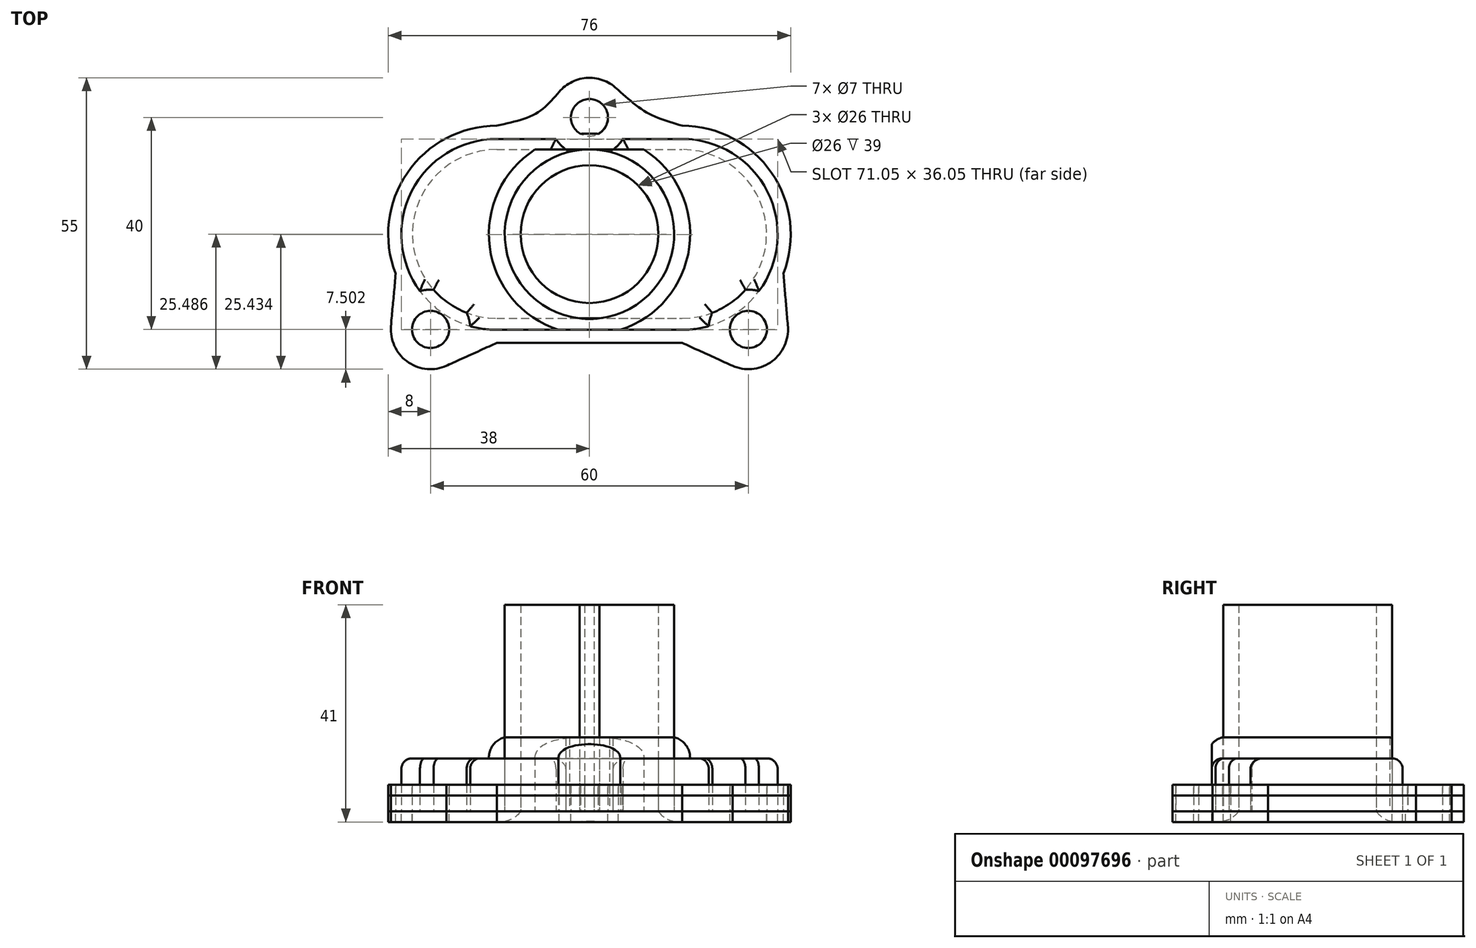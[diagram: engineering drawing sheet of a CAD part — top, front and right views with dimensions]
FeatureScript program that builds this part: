
annotation { "Feature Type Name" : "Feature", "Feature Type Description" : "" }
export const myFeature = defineFeature(function(context is Context, id is Id, definition is map)
    precondition{}
    {
        {
            var Q0;
            Q0=qCreatedBy(makeId("Top.planeOp"),FACE);
            var sketch = newSketch(context, id + "F0", { "sketchPlane" : qUnion([Q0])});
            skCircle(sketch, "E0", {"center": v(0, 24.43) * mm, "radius": 3.5 * mm});
            skCircle(sketch, "E1", {"center": v(30, -15.57) * mm, "radius": 3.5 * mm});
            skCircle(sketch, "E2", {"center": v(-30, -15.57) * mm, "radius": 3.5 * mm});
            skCircle(sketch, "E3", {"center": v(0, 24.43) * mm, "radius": 7.5 * mm});
            skCircle(sketch, "E4", {"center": v(30, -15.57) * mm, "radius": 7.5 * mm});
            skCircle(sketch, "E5", {"center": v(-30, -15.57) * mm, "radius": 7.5 * mm});
            skLineSegment(sketch, "E6", {"start": v(7.34, 22.9) * mm, "end": v(17.5, 22.9) * mm});
            skLineSegment(sketch, "E7", {"start": v(-17.5, -18.1) * mm, "end": v(17.5, -18.1) * mm});
            skLineSegment(sketch, "E8", {"start": v(-7.7, 22.9) * mm, "end": v(-17.5, 22.9) * mm});
            skLineSegment(sketch, "E9", {"start": v(-17.5, 15.9) * mm, "end": v(17.5, 15.9) * mm});
            skLineSegment(sketch, "E10", {"start": v(-17.5, -11.1) * mm, "end": v(17.5, -11.1) * mm});
            skArc(sketch, "E11", {"start": v(17.5, -11.1) * mm, "mid": v(31, 2.4) * mm, "end": v(17.5, 15.9) * mm});
            skArc(sketch, "E12", {"start": v(-17.5, 15.9) * mm, "mid": v(-31, 2.4) * mm, "end": v(-17.5, -11.1) * mm});
            skFitSpline(sketch, "E13", {"points": [v(-17.5, 22.9) * mm, v(-10.03, 25.23) * mm, v(-5.72, 29.28) * mm], "startDerivative": vector(15.12, 3.6) * mm, "endDerivative": vector(8.27, 9.34) * mm});
            skFitSpline(sketch, "E14", {"points": [v(17.5, 22.9) * mm, v(11.1, 25.23) * mm, v(5.4, 29.63) * mm], "startDerivative": vector(-13.33, 4.18) * mm, "endDerivative": vector(-10.87, 9.3) * mm});
            skArc(sketch, "E15", {"start": v(17.5, -18.1) * mm, "mid": v(38, 2.4) * mm, "end": v(17.5, 22.9) * mm});
            skArc(sketch, "E16", {"start": v(-17.5, 22.9) * mm, "mid": v(-38, 2.4) * mm, "end": v(-17.5, -18.1) * mm});
            skFitSpline(sketch, "E17", {"points": [v(27, -22.44) * mm, v(17.5, -18.1) * mm], "startDerivative": vector(-8.6, 4.02) * mm, "endDerivative": vector(-8.6, 4.02) * mm});
            skFitSpline(sketch, "E18", {"points": [v(-17.5, -18.1) * mm, v(-27, -22.44) * mm], "startDerivative": vector(-8, -3.6) * mm, "endDerivative": vector(-8, -3.6) * mm});
            skFitSpline(sketch, "E19", {"points": [v(36.62, -5) * mm, v(37.5, -15.5) * mm], "startDerivative": vector(0.87, -10.65) * mm, "endDerivative": vector(0.87, -10.65) * mm});
            skFitSpline(sketch, "E20", {"points": [v(-37.5, -15.5) * mm, v(-36.62, -5) * mm], "startDerivative": vector(0.62, 11.41) * mm, "endDerivative": vector(0.62, 11.41) * mm});
            skLineSegment(sketch, "E21", {"start": v(-17.5, 20.4) * mm, "end": v(17.5, 20.4) * mm});
            skLineSegment(sketch, "E22", {"start": v(-17.5, -15.66) * mm, "end": v(17.5, -15.66) * mm});
            skArc(sketch, "E23", {"start": v(17.5, -15.66) * mm, "mid": v(35.53, 2.36) * mm, "end": v(17.5, 20.4) * mm});
            skArc(sketch, "E24", {"start": v(-17.5, 20.4) * mm, "mid": v(-35.53, 2.36) * mm, "end": v(-17.5, -15.66) * mm});
            skLineSegment(sketch, "E25", {"start": v(-17.5, 18.4) * mm, "end": v(17.5, 18.4) * mm});
            skLineSegment(sketch, "E26", {"start": v(-17.5, -13.47) * mm, "end": v(17.5, -13.47) * mm});
            skArc(sketch, "E27", {"start": v(17.5, -13.47) * mm, "mid": v(33.43, 2.46) * mm, "end": v(17.5, 18.4) * mm});
            skArc(sketch, "E28", {"start": v(-17.5, 18.4) * mm, "mid": v(-33.43, 2.46) * mm, "end": v(-17.5, -13.47) * mm});
            skCircle(sketch, "E29", {"center": v(0, 2.42) * mm, "radius": 16 * mm});
            skCircle(sketch, "E30", {"center": v(0, 2.42) * mm, "radius": 13 * mm});
            skCircle(sketch, "E31", {"center": v(0, 2.42) * mm, "radius": 19 * mm});
            skSolve(sketch);
        }
        {
            var Q0;
            {var subQ1=sQuery(id+"F0.wireOp",EDGE,"E13");Q0=makeQuery(id+"F0.imprint","IMPRINT",FACE,{"disambiguationData":[TD([[makeQuery(id+"F0.imprint","IMPRINT",EDGE,{"derivedFrom":subQ1}),-1.0]])]});}
            var Q1;
            {var subQ0=sQuery(id+"F0.wireOp",EDGE,"E16");var subQ1=sQuery(id+"F0.wireOp",EDGE,"E2");var subQ2=makeQuery(id+"F0.imprint","INTERSECT",VERTEX,{"disambiguationData":[OD(0.0)],"derivedFrom":[subQ1,subQ0]});Q1=makeQuery(id+"F0.imprint","IMPRINT",FACE,{"disambiguationData":[TD([[makeQuery(id+"F0.imprint","IMPRINT",EDGE,{"disambiguationData":[TD([[subQ2,1.0]])],"derivedFrom":subQ1}),-1.0]])]});}
            var Q2;
            {var subQ6=sQuery(id+"F0.wireOp",EDGE,"E7");Q2=makeQuery(id+"F0.imprint","IMPRINT",FACE,{"disambiguationData":[TD([[makeQuery(id+"F0.imprint","IMPRINT",EDGE,{"derivedFrom":subQ6}),1.0]])]});}
            var Q3;
            {var subQ0=sQuery(id+"F0.wireOp",EDGE,"E18");var subQ1=sQuery(id+"F0.wireOp",EDGE,"E5");var subQ2=makeQuery(id+"F0.imprint","INTERSECT",VERTEX,{"disambiguationData":[OD(1.0)],"derivedFrom":[subQ1,subQ0]});Q3=makeQuery(id+"F0.imprint","IMPRINT",FACE,{"disambiguationData":[TD([[makeQuery(id+"F0.imprint","IMPRINT",EDGE,{"disambiguationData":[TD([[subQ2,-1.0]])],"derivedFrom":subQ1}),-1.0]])]});}
            var Q4;
            {var subQ6=sQuery(id+"F0.wireOp",EDGE,"E16");var subQ10=sQuery(id+"F0.wireOp",EDGE,"E2");var subQ11=makeQuery(id+"F0.imprint","INTERSECT",VERTEX,{"disambiguationData":[OD(0.0)],"derivedFrom":[subQ10,subQ6]});Q4=makeQuery(id+"F0.imprint","IMPRINT",FACE,{"disambiguationData":[TD([[makeQuery(id+"F0.imprint","IMPRINT",EDGE,{"disambiguationData":[TD([[subQ11,-1.0]])],"derivedFrom":subQ10}),-1.0]])]});}
            var Q5;
            {var subQ0=sQuery(id+"F0.wireOp",EDGE,"E20");var subQ1=sQuery(id+"F0.wireOp",EDGE,"E5");var subQ2=makeQuery(id+"F0.imprint","INTERSECT",VERTEX,{"disambiguationData":[OD(1.0)],"derivedFrom":[subQ1,subQ0]});Q5=makeQuery(id+"F0.imprint","IMPRINT",FACE,{"disambiguationData":[TD([[makeQuery(id+"F0.imprint","IMPRINT",EDGE,{"disambiguationData":[TD([[subQ2,1.0]])],"derivedFrom":subQ1}),-1.0]])]});}
            var Q6;
            {var subQ0=sQuery(id+"F0.wireOp",EDGE,"E6");Q6=makeQuery(id+"F0.imprint","IMPRINT",FACE,{"disambiguationData":[TD([[makeQuery(id+"F0.imprint","IMPRINT",EDGE,{"derivedFrom":subQ0}),1.0]])]});}
            var Q7;
            {var subQ0=sQuery(id+"F0.wireOp",EDGE,"E6");Q7=makeQuery(id+"F0.imprint","IMPRINT",FACE,{"disambiguationData":[TD([[makeQuery(id+"F0.imprint","IMPRINT",EDGE,{"derivedFrom":subQ0}),-1.0]])]});}
            var Q8;
            {var subQ0=sQuery(id+"F0.wireOp",EDGE,"E19");var subQ1=sQuery(id+"F0.wireOp",EDGE,"E4");var subQ2=makeQuery(id+"F0.imprint","INTERSECT",VERTEX,{"disambiguationData":[OD(1.0)],"derivedFrom":[subQ1,subQ0]});Q8=makeQuery(id+"F0.imprint","IMPRINT",FACE,{"disambiguationData":[TD([[makeQuery(id+"F0.imprint","IMPRINT",EDGE,{"disambiguationData":[TD([[subQ2,-1.0]])],"derivedFrom":subQ1}),-1.0]])]});}
            var Q9;
            {var subQ6=sQuery(id+"F0.wireOp",EDGE,"E15");var subQ10=sQuery(id+"F0.wireOp",EDGE,"E1");var subQ12=makeQuery(id+"F0.imprint","INTERSECT",VERTEX,{"disambiguationData":[OD(0.0)],"derivedFrom":[subQ10,subQ6]});Q9=makeQuery(id+"F0.imprint","IMPRINT",FACE,{"disambiguationData":[TD([[makeQuery(id+"F0.imprint","IMPRINT",EDGE,{"disambiguationData":[TD([[subQ12,-1.0]])],"derivedFrom":subQ10}),-1.0]])]});}
            var Q10;
            {var subQ0=sQuery(id+"F0.wireOp",EDGE,"E17");var subQ1=sQuery(id+"F0.wireOp",EDGE,"E4");var subQ2=makeQuery(id+"F0.imprint","INTERSECT",VERTEX,{"disambiguationData":[OD(1.0)],"derivedFrom":[subQ1,subQ0]});Q10=makeQuery(id+"F0.imprint","IMPRINT",FACE,{"disambiguationData":[TD([[makeQuery(id+"F0.imprint","IMPRINT",EDGE,{"disambiguationData":[TD([[subQ2,1.0]])],"derivedFrom":subQ1}),-1.0]])]});}
            var Q11;
            {var subQ0=sQuery(id+"F0.wireOp",EDGE,"E15");var subQ5=sQuery(id+"F0.wireOp",EDGE,"E1");var subQ6=makeQuery(id+"F0.imprint","INTERSECT",VERTEX,{"disambiguationData":[OD(0.0)],"derivedFrom":[subQ5,subQ0]});Q11=makeQuery(id+"F0.imprint","IMPRINT",FACE,{"disambiguationData":[TD([[makeQuery(id+"F0.imprint","IMPRINT",EDGE,{"disambiguationData":[TD([[subQ6,1.0]])],"derivedFrom":subQ5}),-1.0]])]});}
            var Q12;
            {var subQ0=sQuery(id+"F0.wireOp",EDGE,"E25");var subQ1=sQuery(id+"F0.wireOp",EDGE,"E3");var subQ2=makeQuery(id+"F0.imprint","INTERSECT",VERTEX,{"disambiguationData":[OD(0.0)],"derivedFrom":[subQ1,subQ0]});Q12=makeQuery(id+"F0.imprint","IMPRINT",FACE,{"disambiguationData":[TD([[makeQuery(id+"F0.imprint","IMPRINT",EDGE,{"disambiguationData":[TD([[subQ2,-1.0]])],"derivedFrom":subQ1}),1.0]])]});}
            var Q13;
            {var subQ0=sQuery(id+"F0.wireOp",EDGE,"E28");var subQ1=sQuery(id+"F0.wireOp",EDGE,"E5");var subQ2=makeQuery(id+"F0.imprint","INTERSECT",VERTEX,{"disambiguationData":[OD(0.0)],"derivedFrom":[subQ1,subQ0]});Q13=makeQuery(id+"F0.imprint","IMPRINT",FACE,{"disambiguationData":[TD([[makeQuery(id+"F0.imprint","IMPRINT",EDGE,{"disambiguationData":[TD([[subQ2,-1.0]])],"derivedFrom":subQ1}),1.0]])]});}
            var Q14;
            {var subQ0=sQuery(id+"F0.wireOp",EDGE,"E27");var subQ1=sQuery(id+"F0.wireOp",EDGE,"E4");var subQ2=makeQuery(id+"F0.imprint","INTERSECT",VERTEX,{"disambiguationData":[OD(0.0)],"derivedFrom":[subQ1,subQ0]});Q14=makeQuery(id+"F0.imprint","IMPRINT",FACE,{"disambiguationData":[TD([[makeQuery(id+"F0.imprint","IMPRINT",EDGE,{"disambiguationData":[TD([[subQ2,-1.0]])],"derivedFrom":subQ1}),1.0]])]});}
            var Q15;
            {var subQ0=sQuery(id+"F0.wireOp",EDGE,"E21");var subQ1=sQuery(id+"F0.wireOp",EDGE,"E3");var subQ2=makeQuery(id+"F0.imprint","INTERSECT",VERTEX,{"disambiguationData":[OD(0.0)],"derivedFrom":[subQ1,subQ0]});Q15=makeQuery(id+"F0.imprint","IMPRINT",FACE,{"disambiguationData":[TD([[makeQuery(id+"F0.imprint","IMPRINT",EDGE,{"disambiguationData":[TD([[subQ2,-1.0]])],"derivedFrom":subQ1}),1.0]])]});}
            var Q16;
            {var subQ0=sQuery(id+"F0.wireOp",EDGE,"E12");Q16=makeQuery(id+"F0.imprint","IMPRINT",FACE,{"disambiguationData":[TD([[makeQuery(id+"F0.imprint","IMPRINT",EDGE,{"derivedFrom":subQ0}),-1.0]])]});}
            var Q17;
            {var subQ0=sQuery(id+"F0.wireOp",EDGE,"E11");Q17=makeQuery(id+"F0.imprint","IMPRINT",FACE,{"disambiguationData":[TD([[makeQuery(id+"F0.imprint","IMPRINT",EDGE,{"derivedFrom":subQ0}),-1.0]])]});}
            var Q18;
            {var subQ0=sQuery(id+"F0.wireOp",EDGE,"E29");var subQ1=sQuery(id+"F0.wireOp",EDGE,"E3");var subQ2=makeQuery(id+"F0.imprint","INTERSECT",VERTEX,{"disambiguationData":[OD(0.0)],"derivedFrom":[subQ1,subQ0]});Q18=makeQuery(id+"F0.imprint","IMPRINT",FACE,{"disambiguationData":[TD([[makeQuery(id+"F0.imprint","IMPRINT",EDGE,{"disambiguationData":[TD([[subQ2,-1.0]])],"derivedFrom":subQ1}),-1.0]])]});}
            var Q19;
            {var subQ0=sQuery(id+"F0.wireOp",EDGE,"E29");var subQ1=sQuery(id+"F0.wireOp",EDGE,"E3");var subQ2=makeQuery(id+"F0.imprint","INTERSECT",VERTEX,{"disambiguationData":[OD(0.0)],"derivedFrom":[subQ1,subQ0]});Q19=makeQuery(id+"F0.imprint","IMPRINT",FACE,{"disambiguationData":[TD([[makeQuery(id+"F0.imprint","IMPRINT",EDGE,{"disambiguationData":[TD([[subQ2,-1.0]])],"derivedFrom":subQ1}),1.0]])]});}
            var Q20;
            {var subQ0=sQuery(id+"F0.wireOp",EDGE,"E29");var subQ1=sQuery(id+"F0.wireOp",EDGE,"E3");var subQ2=makeQuery(id+"F0.imprint","INTERSECT",VERTEX,{"disambiguationData":[OD(1.0)],"derivedFrom":[subQ1,subQ0]});Q20=makeQuery(id+"F0.imprint","IMPRINT",FACE,{"disambiguationData":[TD([[makeQuery(id+"F0.imprint","IMPRINT",EDGE,{"disambiguationData":[TD([[subQ2,-1.0]])],"derivedFrom":subQ1}),1.0]])]});}
            var Q21;
            {var subQ0=sQuery(id+"F0.wireOp",EDGE,"E11");Q21=makeQuery(id+"F0.imprint","IMPRINT",FACE,{"disambiguationData":[TD([[makeQuery(id+"F0.imprint","IMPRINT",EDGE,{"derivedFrom":subQ0}),1.0]])]});}
            var Q22;
            {var subQ0=sQuery(id+"F0.wireOp",EDGE,"E12");Q22=makeQuery(id+"F0.imprint","IMPRINT",FACE,{"disambiguationData":[TD([[makeQuery(id+"F0.imprint","IMPRINT",EDGE,{"derivedFrom":subQ0}),1.0]])]});}
            var Q23;
            Q23=makeQuery(id+"F0.imprint","IMPRINT",FACE,{"disambiguationData":[TD([[makeQuery(id+"F0.imprint","IMPRINT",EDGE,{"derivedFrom":sQuery(id+"F0.wireOp",EDGE,"E30")}),-1.0]])]});
            var Q24;
            {var subQ0=sQuery(id+"F0.wireOp",EDGE,"E29");var subQ1=sQuery(id+"F0.wireOp",EDGE,"E10");var subQ2=makeQuery(id+"F0.imprint","INTERSECT",VERTEX,{"disambiguationData":[OD(0.0)],"derivedFrom":[subQ1,subQ0]});Q24=makeQuery(id+"F0.imprint","IMPRINT",FACE,{"disambiguationData":[TD([[makeQuery(id+"F0.imprint","IMPRINT",EDGE,{"disambiguationData":[TD([[subQ2,-1.0]])],"derivedFrom":subQ1}),-1.0]])]});}
            var Q25;
            {var subQ0=sQuery(id+"F0.wireOp",EDGE,"E31");var subQ1=sQuery(id+"F0.wireOp",EDGE,"E22");var subQ2=makeQuery(id+"F0.imprint","INTERSECT",VERTEX,{"disambiguationData":[OD(0.0)],"derivedFrom":[subQ1,subQ0]});Q25=makeQuery(id+"F0.imprint","IMPRINT",FACE,{"disambiguationData":[TD([[makeQuery(id+"F0.imprint","IMPRINT",EDGE,{"disambiguationData":[TD([[subQ2,-1.0]])],"derivedFrom":subQ1}),-1.0]])]});}
            var Q26;
            {var subQ0=sQuery(id+"F0.wireOp",EDGE,"E29");var subQ1=sQuery(id+"F0.wireOp",EDGE,"E9");var subQ2=makeQuery(id+"F0.imprint","INTERSECT",VERTEX,{"disambiguationData":[OD(1.0)],"derivedFrom":[subQ1,subQ0]});Q26=makeQuery(id+"F0.imprint","IMPRINT",FACE,{"disambiguationData":[TD([[makeQuery(id+"F0.imprint","IMPRINT",EDGE,{"disambiguationData":[TD([[subQ2,-1.0]])],"derivedFrom":subQ1}),-1.0]])]});}
            var Q27;
            {var subQ0=sQuery(id+"F0.wireOp",EDGE,"E31");var subQ1=sQuery(id+"F0.wireOp",EDGE,"E9");var subQ2=makeQuery(id+"F0.imprint","INTERSECT",VERTEX,{"disambiguationData":[OD(0.0)],"derivedFrom":[subQ1,subQ0]});Q27=makeQuery(id+"F0.imprint","IMPRINT",FACE,{"disambiguationData":[TD([[makeQuery(id+"F0.imprint","IMPRINT",EDGE,{"disambiguationData":[TD([[subQ2,-1.0]])],"derivedFrom":subQ1}),-1.0]])]});}
            var Q28;
            {var subQ0=sQuery(id+"F0.wireOp",EDGE,"E31");var subQ1=sQuery(id+"F0.wireOp",EDGE,"E10");var subQ2=makeQuery(id+"F0.imprint","INTERSECT",VERTEX,{"disambiguationData":[OD(0.0)],"derivedFrom":[subQ1,subQ0]});Q28=makeQuery(id+"F0.imprint","IMPRINT",FACE,{"disambiguationData":[TD([[makeQuery(id+"F0.imprint","IMPRINT",EDGE,{"disambiguationData":[TD([[subQ2,-1.0]])],"derivedFrom":subQ1}),-1.0]])]});}
            var Q29;
            {var subQ0=sQuery(id+"F0.wireOp",EDGE,"E29");var subQ1=sQuery(id+"F0.wireOp",EDGE,"E10");var subQ2=makeQuery(id+"F0.imprint","INTERSECT",VERTEX,{"disambiguationData":[OD(1.0)],"derivedFrom":[subQ1,subQ0]});Q29=makeQuery(id+"F0.imprint","IMPRINT",FACE,{"disambiguationData":[TD([[makeQuery(id+"F0.imprint","IMPRINT",EDGE,{"disambiguationData":[TD([[subQ2,-1.0]])],"derivedFrom":subQ1}),-1.0]])]});}
            var Q30;
            {var subQ1=sQuery(id+"F0.wireOp",EDGE,"E3");var subQ7=sQuery(id+"F0.wireOp",EDGE,"E25");var subQ8=makeQuery(id+"F0.imprint","INTERSECT",VERTEX,{"disambiguationData":[OD(0.0)],"derivedFrom":[subQ1,subQ7]});Q30=makeQuery(id+"F0.imprint","IMPRINT",FACE,{"disambiguationData":[TD([[makeQuery(id+"F0.imprint","IMPRINT",EDGE,{"disambiguationData":[TD([[subQ8,-1.0]])],"derivedFrom":subQ1}),-1.0]])]});}
            var Q31;
            {var subQ1=sQuery(id+"F0.wireOp",EDGE,"E3");var subQ5=sQuery(id+"F0.wireOp",EDGE,"E29");var subQ6=makeQuery(id+"F0.imprint","INTERSECT",VERTEX,{"disambiguationData":[OD(1.0)],"derivedFrom":[subQ1,subQ5]});Q31=makeQuery(id+"F0.imprint","IMPRINT",FACE,{"disambiguationData":[TD([[makeQuery(id+"F0.imprint","IMPRINT",EDGE,{"disambiguationData":[TD([[subQ6,-1.0]])],"derivedFrom":subQ1}),-1.0]])]});}
            var Q32;
            {var subQ7=sQuery(id+"F0.wireOp",EDGE,"E31");var subQ8=sQuery(id+"F0.wireOp",EDGE,"E0");var subQ9=makeQuery(id+"F0.imprint","INTERSECT",VERTEX,{"disambiguationData":[OD(0.0)],"derivedFrom":[subQ8,subQ7]});Q32=makeQuery(id+"F0.imprint","IMPRINT",FACE,{"disambiguationData":[TD([[makeQuery(id+"F0.imprint","IMPRINT",EDGE,{"disambiguationData":[TD([[subQ9,-1.0]])],"derivedFrom":subQ8}),-1.0]])]});}
            var Q33;
            {var subQ0=sQuery(id+"F0.wireOp",EDGE,"E31");var subQ1=sQuery(id+"F0.wireOp",EDGE,"E0");var subQ2=makeQuery(id+"F0.imprint","INTERSECT",VERTEX,{"disambiguationData":[OD(0.0)],"derivedFrom":[subQ1,subQ0]});Q33=makeQuery(id+"F0.imprint","IMPRINT",FACE,{"disambiguationData":[TD([[makeQuery(id+"F0.imprint","IMPRINT",EDGE,{"disambiguationData":[TD([[subQ2,1.0]])],"derivedFrom":subQ1}),1.0]])]});}
            var Q34;
            {var subQ0=sQuery(id+"F0.wireOp",EDGE,"E31");var subQ1=sQuery(id+"F0.wireOp",EDGE,"E0");var subQ2=makeQuery(id+"F0.imprint","INTERSECT",VERTEX,{"disambiguationData":[OD(0.0)],"derivedFrom":[subQ1,subQ0]});Q34=makeQuery(id+"F0.imprint","IMPRINT",FACE,{"disambiguationData":[TD([[makeQuery(id+"F0.imprint","IMPRINT",EDGE,{"disambiguationData":[TD([[subQ2,1.0]])],"derivedFrom":subQ1}),-1.0]])]});}
            var Q35;
            {var subQ0=sQuery(id+"F0.wireOp",EDGE,"E29");var subQ1=sQuery(id+"F0.wireOp",EDGE,"E26");var subQ2=makeQuery(id+"F0.imprint","INTERSECT",VERTEX,{"disambiguationData":[OD(0.0)],"derivedFrom":[subQ1,subQ0]});Q35=makeQuery(id+"F0.imprint","IMPRINT",FACE,{"disambiguationData":[TD([[makeQuery(id+"F0.imprint","IMPRINT",EDGE,{"disambiguationData":[TD([[subQ2,-1.0]])],"derivedFrom":subQ1}),-1.0]])]});}
            var Q36;
            {var subQ3=sQuery(id+"F0.wireOp",EDGE,"E5");var subQ5=sQuery(id+"F0.wireOp",EDGE,"E28");var subQ11=makeQuery(id+"F0.imprint","INTERSECT",VERTEX,{"disambiguationData":[OD(0.0)],"derivedFrom":[subQ3,subQ5]});Q36=makeQuery(id+"F0.imprint","IMPRINT",FACE,{"disambiguationData":[TD([[makeQuery(id+"F0.imprint","IMPRINT",EDGE,{"disambiguationData":[TD([[subQ11,1.0]])],"derivedFrom":subQ3}),-1.0]])]});}
            var Q37;
            {var subQ4=sQuery(id+"F0.wireOp",EDGE,"E31");var subQ7=sQuery(id+"F0.wireOp",EDGE,"E22");var subQ9=makeQuery(id+"F0.imprint","INTERSECT",VERTEX,{"disambiguationData":[OD(0.0)],"derivedFrom":[subQ7,subQ4]});Q37=makeQuery(id+"F0.imprint","IMPRINT",FACE,{"disambiguationData":[TD([[makeQuery(id+"F0.imprint","IMPRINT",EDGE,{"disambiguationData":[TD([[subQ9,-1.0]])],"derivedFrom":subQ7}),1.0]])]});}
            var Q38;
            {var subQ0=sQuery(id+"F0.wireOp",EDGE,"E27");var subQ9=sQuery(id+"F0.wireOp",EDGE,"E4");var subQ11=makeQuery(id+"F0.imprint","INTERSECT",VERTEX,{"disambiguationData":[OD(1.0)],"derivedFrom":[subQ9,subQ0]});Q38=makeQuery(id+"F0.imprint","IMPRINT",FACE,{"disambiguationData":[TD([[makeQuery(id+"F0.imprint","IMPRINT",EDGE,{"disambiguationData":[TD([[subQ11,-1.0]])],"derivedFrom":subQ9}),-1.0]])]});}
            var Q39;
            {var subQ0=sQuery(id+"F0.wireOp",EDGE,"E23");var subQ1=sQuery(id+"F0.wireOp",EDGE,"E4");var subQ2=makeQuery(id+"F0.imprint","INTERSECT",VERTEX,{"disambiguationData":[OD(0.0)],"derivedFrom":[subQ1,subQ0]});Q39=makeQuery(id+"F0.imprint","IMPRINT",FACE,{"disambiguationData":[TD([[makeQuery(id+"F0.imprint","IMPRINT",EDGE,{"disambiguationData":[TD([[subQ2,-1.0]])],"derivedFrom":subQ1}),1.0]])]});}
            var Q40;
            {var subQ7=sQuery(id+"F0.wireOp",EDGE,"E3");var subQ9=sQuery(id+"F0.wireOp",EDGE,"E31");var subQ10=makeQuery(id+"F0.imprint","INTERSECT",VERTEX,{"disambiguationData":[OD(1.0)],"derivedFrom":[subQ7,subQ9]});Q40=makeQuery(id+"F0.imprint","IMPRINT",FACE,{"disambiguationData":[TD([[makeQuery(id+"F0.imprint","IMPRINT",EDGE,{"disambiguationData":[TD([[subQ10,-1.0]])],"derivedFrom":subQ7}),-1.0]])]});}
            var Q41;
            {var subQ0=sQuery(id+"F0.wireOp",EDGE,"E28");var subQ1=sQuery(id+"F0.wireOp",EDGE,"E5");var subQ2=makeQuery(id+"F0.imprint","INTERSECT",VERTEX,{"disambiguationData":[OD(0.0)],"derivedFrom":[subQ1,subQ0]});Q41=makeQuery(id+"F0.imprint","IMPRINT",FACE,{"disambiguationData":[TD([[makeQuery(id+"F0.imprint","IMPRINT",EDGE,{"disambiguationData":[TD([[subQ2,1.0]])],"derivedFrom":subQ1}),1.0]])]});}
            var Q42;
            {var subQ1=sQuery(id+"F0.wireOp",EDGE,"E21");var subQ5=sQuery(id+"F0.wireOp",EDGE,"E3");var subQ6=makeQuery(id+"F0.imprint","INTERSECT",VERTEX,{"disambiguationData":[OD(0.0)],"derivedFrom":[subQ5,subQ1]});Q42=makeQuery(id+"F0.imprint","IMPRINT",FACE,{"disambiguationData":[TD([[makeQuery(id+"F0.imprint","IMPRINT",EDGE,{"disambiguationData":[TD([[subQ6,-1.0]])],"derivedFrom":subQ5}),-1.0]])]});}
            var Q43;
            {var subQ0=sQuery(id+"F0.wireOp",EDGE,"E31");var subQ1=sQuery(id+"F0.wireOp",EDGE,"E3");var subQ2=makeQuery(id+"F0.imprint","INTERSECT",VERTEX,{"disambiguationData":[OD(0.0)],"derivedFrom":[subQ1,subQ0]});Q43=makeQuery(id+"F0.imprint","IMPRINT",FACE,{"disambiguationData":[TD([[makeQuery(id+"F0.imprint","IMPRINT",EDGE,{"disambiguationData":[TD([[subQ2,-1.0]])],"derivedFrom":subQ1}),-1.0]])]});}
            var Q44;
            {var subQ1=sQuery(id+"F0.wireOp",EDGE,"E3");var subQ6=sQuery(id+"F0.wireOp",EDGE,"E31");var subQ12=makeQuery(id+"F0.imprint","INTERSECT",VERTEX,{"disambiguationData":[OD(0.0)],"derivedFrom":[subQ1,subQ6]});Q44=makeQuery(id+"F0.imprint","IMPRINT",FACE,{"disambiguationData":[TD([[makeQuery(id+"F0.imprint","IMPRINT",EDGE,{"disambiguationData":[TD([[subQ12,-1.0]])],"derivedFrom":subQ1}),1.0]])]});}
            var Q45;
            {var subQ0=sQuery(id+"F0.wireOp",EDGE,"E25");var subQ1=sQuery(id+"F0.wireOp",EDGE,"E3");var subQ2=makeQuery(id+"F0.imprint","INTERSECT",VERTEX,{"disambiguationData":[OD(1.0)],"derivedFrom":[subQ1,subQ0]});Q45=makeQuery(id+"F0.imprint","IMPRINT",FACE,{"disambiguationData":[TD([[makeQuery(id+"F0.imprint","IMPRINT",EDGE,{"disambiguationData":[TD([[subQ2,-1.0]])],"derivedFrom":subQ1}),-1.0]])]});}
            extrude(context, id + "F1", {"entities" : qUnion([Q0, Q1, Q2, Q3, Q4, Q5, Q6, Q7, Q8, Q9, Q10, Q11, Q12, Q13, Q14, Q15, Q16, Q17, Q18, Q19, Q20, Q21, Q22, Q23, Q24, Q25, Q26, Q27, Q28, Q29, Q30, Q31, Q32, Q33, Q34, Q35, Q36, Q37, Q38, Q39, Q40, Q41, Q42, Q43, Q44, Q45]), "depth" : 5 * mm});
        }
        {
            var Q0;
            {var subQ0=sQuery(id+"F0.wireOp",EDGE,"E18");var subQ1=sQuery(id+"F0.wireOp",EDGE,"E5");var subQ2=makeQuery(id+"F0.imprint","INTERSECT",VERTEX,{"disambiguationData":[OD(1.0)],"derivedFrom":[subQ1,subQ0]});Q0=makeQuery(id+"F0.imprint","IMPRINT",FACE,{"disambiguationData":[TD([[makeQuery(id+"F0.imprint","IMPRINT",EDGE,{"disambiguationData":[TD([[subQ2,-1.0]])],"derivedFrom":subQ1}),-1.0]])]});}
            var Q1;
            {var subQ3=sQuery(id+"F0.wireOp",EDGE,"E16");var subQ5=sQuery(id+"F0.wireOp",EDGE,"E2");var subQ6=makeQuery(id+"F0.imprint","INTERSECT",VERTEX,{"disambiguationData":[OD(0.0)],"derivedFrom":[subQ5,subQ3]});Q1=makeQuery(id+"F0.imprint","IMPRINT",FACE,{"disambiguationData":[TD([[makeQuery(id+"F0.imprint","IMPRINT",EDGE,{"disambiguationData":[TD([[subQ6,-1.0]])],"derivedFrom":subQ5}),-1.0]])]});}
            var Q2;
            {var subQ0=sQuery(id+"F0.wireOp",EDGE,"E16");var subQ1=sQuery(id+"F0.wireOp",EDGE,"E2");var subQ2=makeQuery(id+"F0.imprint","INTERSECT",VERTEX,{"disambiguationData":[OD(0.0)],"derivedFrom":[subQ1,subQ0]});Q2=makeQuery(id+"F0.imprint","IMPRINT",FACE,{"disambiguationData":[TD([[makeQuery(id+"F0.imprint","IMPRINT",EDGE,{"disambiguationData":[TD([[subQ2,1.0]])],"derivedFrom":subQ1}),-1.0]])]});}
            var Q3;
            {var subQ1=sQuery(id+"F0.wireOp",EDGE,"E7");Q3=makeQuery(id+"F0.imprint","IMPRINT",FACE,{"disambiguationData":[TD([[makeQuery(id+"F0.imprint","IMPRINT",EDGE,{"derivedFrom":subQ1}),1.0]])]});}
            var Q4;
            {var subQ0=sQuery(id+"F0.wireOp",EDGE,"E25");var subQ1=sQuery(id+"F0.wireOp",EDGE,"E3");var subQ2=makeQuery(id+"F0.imprint","INTERSECT",VERTEX,{"disambiguationData":[OD(0.0)],"derivedFrom":[subQ1,subQ0]});Q4=makeQuery(id+"F0.imprint","IMPRINT",FACE,{"disambiguationData":[TD([[makeQuery(id+"F0.imprint","IMPRINT",EDGE,{"disambiguationData":[TD([[subQ2,-1.0]])],"derivedFrom":subQ1}),1.0]])]});}
            var Q5;
            {var subQ0=sQuery(id+"F0.wireOp",EDGE,"E28");var subQ1=sQuery(id+"F0.wireOp",EDGE,"E5");var subQ2=makeQuery(id+"F0.imprint","INTERSECT",VERTEX,{"disambiguationData":[OD(0.0)],"derivedFrom":[subQ1,subQ0]});Q5=makeQuery(id+"F0.imprint","IMPRINT",FACE,{"disambiguationData":[TD([[makeQuery(id+"F0.imprint","IMPRINT",EDGE,{"disambiguationData":[TD([[subQ2,-1.0]])],"derivedFrom":subQ1}),1.0]])]});}
            var Q6;
            Q6=makeQuery(id+"F0.imprint","IMPRINT",FACE,{"disambiguationData":[TD([[makeQuery(id+"F0.imprint","IMPRINT",EDGE,{"derivedFrom":sQuery(id+"F0.wireOp",EDGE,"E9")}),1.0]])]});
            var Q7;
            {var subQ0=sQuery(id+"F0.wireOp",EDGE,"E27");var subQ1=sQuery(id+"F0.wireOp",EDGE,"E4");var subQ2=makeQuery(id+"F0.imprint","INTERSECT",VERTEX,{"disambiguationData":[OD(0.0)],"derivedFrom":[subQ1,subQ0]});Q7=makeQuery(id+"F0.imprint","IMPRINT",FACE,{"disambiguationData":[TD([[makeQuery(id+"F0.imprint","IMPRINT",EDGE,{"disambiguationData":[TD([[subQ2,-1.0]])],"derivedFrom":subQ1}),1.0]])]});}
            var Q8;
            {var subQ0=sQuery(id+"F0.wireOp",EDGE,"E6");Q8=makeQuery(id+"F0.imprint","IMPRINT",FACE,{"disambiguationData":[TD([[makeQuery(id+"F0.imprint","IMPRINT",EDGE,{"derivedFrom":subQ0}),-1.0]])]});}
            var Q9;
            Q9=makeQuery(id+"F0.imprint","IMPRINT",FACE,{"disambiguationData":[TD([[makeQuery(id+"F0.imprint","IMPRINT",EDGE,{"derivedFrom":sQuery(id+"F0.wireOp",EDGE,"E0")}),-1.0]])]});
            var Q10;
            {var subQ0=sQuery(id+"F0.wireOp",EDGE,"E6");Q10=makeQuery(id+"F0.imprint","IMPRINT",FACE,{"disambiguationData":[TD([[makeQuery(id+"F0.imprint","IMPRINT",EDGE,{"derivedFrom":subQ0}),1.0]])]});}
            var Q11;
            {var subQ1=sQuery(id+"F0.wireOp",EDGE,"E13");Q11=makeQuery(id+"F0.imprint","IMPRINT",FACE,{"disambiguationData":[TD([[makeQuery(id+"F0.imprint","IMPRINT",EDGE,{"derivedFrom":subQ1}),-1.0]])]});}
            var Q12;
            {var subQ0=sQuery(id+"F0.wireOp",EDGE,"E15");var subQ1=sQuery(id+"F0.wireOp",EDGE,"E1");var subQ2=makeQuery(id+"F0.imprint","INTERSECT",VERTEX,{"disambiguationData":[OD(0.0)],"derivedFrom":[subQ1,subQ0]});Q12=makeQuery(id+"F0.imprint","IMPRINT",FACE,{"disambiguationData":[TD([[makeQuery(id+"F0.imprint","IMPRINT",EDGE,{"disambiguationData":[TD([[subQ2,1.0]])],"derivedFrom":subQ1}),-1.0]])]});}
            var Q13;
            {var subQ6=sQuery(id+"F0.wireOp",EDGE,"E15");var subQ10=sQuery(id+"F0.wireOp",EDGE,"E1");var subQ11=makeQuery(id+"F0.imprint","INTERSECT",VERTEX,{"disambiguationData":[OD(0.0)],"derivedFrom":[subQ10,subQ6]});Q13=makeQuery(id+"F0.imprint","IMPRINT",FACE,{"disambiguationData":[TD([[makeQuery(id+"F0.imprint","IMPRINT",EDGE,{"disambiguationData":[TD([[subQ11,-1.0]])],"derivedFrom":subQ10}),-1.0]])]});}
            var Q14;
            {var subQ0=sQuery(id+"F0.wireOp",EDGE,"E19");var subQ1=sQuery(id+"F0.wireOp",EDGE,"E4");var subQ2=makeQuery(id+"F0.imprint","INTERSECT",VERTEX,{"disambiguationData":[OD(1.0)],"derivedFrom":[subQ1,subQ0]});Q14=makeQuery(id+"F0.imprint","IMPRINT",FACE,{"disambiguationData":[TD([[makeQuery(id+"F0.imprint","IMPRINT",EDGE,{"disambiguationData":[TD([[subQ2,-1.0]])],"derivedFrom":subQ1}),-1.0]])]});}
            var Q15;
            {var subQ0=sQuery(id+"F0.wireOp",EDGE,"E17");var subQ1=sQuery(id+"F0.wireOp",EDGE,"E4");var subQ2=makeQuery(id+"F0.imprint","INTERSECT",VERTEX,{"disambiguationData":[OD(1.0)],"derivedFrom":[subQ1,subQ0]});Q15=makeQuery(id+"F0.imprint","IMPRINT",FACE,{"disambiguationData":[TD([[makeQuery(id+"F0.imprint","IMPRINT",EDGE,{"disambiguationData":[TD([[subQ2,1.0]])],"derivedFrom":subQ1}),-1.0]])]});}
            var Q16;
            {var subQ0=sQuery(id+"F0.wireOp",EDGE,"E20");var subQ1=sQuery(id+"F0.wireOp",EDGE,"E5");var subQ2=makeQuery(id+"F0.imprint","INTERSECT",VERTEX,{"disambiguationData":[OD(1.0)],"derivedFrom":[subQ1,subQ0]});Q16=makeQuery(id+"F0.imprint","IMPRINT",FACE,{"disambiguationData":[TD([[makeQuery(id+"F0.imprint","IMPRINT",EDGE,{"disambiguationData":[TD([[subQ2,1.0]])],"derivedFrom":subQ1}),-1.0]])]});}
            var Q17;
            {var subQ0=sQuery(id+"F0.wireOp",EDGE,"E29");var subQ1=sQuery(id+"F0.wireOp",EDGE,"E10");var subQ2=makeQuery(id+"F0.imprint","INTERSECT",VERTEX,{"disambiguationData":[OD(0.0)],"derivedFrom":[subQ1,subQ0]});Q17=makeQuery(id+"F0.imprint","IMPRINT",FACE,{"disambiguationData":[TD([[makeQuery(id+"F0.imprint","IMPRINT",EDGE,{"disambiguationData":[TD([[subQ2,-1.0]])],"derivedFrom":subQ1}),-1.0]])]});}
            var Q18;
            {var subQ15=sQuery(id+"F0.wireOp",EDGE,"E12");Q18=makeQuery(id+"F0.imprint","IMPRINT",FACE,{"disambiguationData":[TD([[makeQuery(id+"F0.imprint","IMPRINT",EDGE,{"derivedFrom":subQ15}),-1.0]])]});}
            var Q19;
            {var subQ0=sQuery(id+"F0.wireOp",EDGE,"E29");var subQ1=sQuery(id+"F0.wireOp",EDGE,"E3");var subQ2=makeQuery(id+"F0.imprint","INTERSECT",VERTEX,{"disambiguationData":[OD(0.0)],"derivedFrom":[subQ1,subQ0]});Q19=makeQuery(id+"F0.imprint","IMPRINT",FACE,{"disambiguationData":[TD([[makeQuery(id+"F0.imprint","IMPRINT",EDGE,{"disambiguationData":[TD([[subQ2,-1.0]])],"derivedFrom":subQ1}),1.0]])]});}
            var Q20;
            Q20=makeQuery(id+"F1.opExtrude","CAP_FACE",FACE,{"disambiguationData":[OSD([sQuery(id+"F0.wireOp",EDGE,"E0"),sQuery(id+"F0.wireOp",EDGE,"E1"),sQuery(id+"F0.wireOp",EDGE,"E2"),sQuery(id+"F0.wireOp",EDGE,"E3"),sQuery(id+"F0.wireOp",EDGE,"E4"),sQuery(id+"F0.wireOp",EDGE,"E5"),sQuery(id+"F0.wireOp",EDGE,"E7"),sQuery(id+"F0.wireOp",EDGE,"E13"),sQuery(id+"F0.wireOp",EDGE,"E14"),sQuery(id+"F0.wireOp",EDGE,"E15"),sQuery(id+"F0.wireOp",EDGE,"E16"),sQuery(id+"F0.wireOp",EDGE,"E17"),sQuery(id+"F0.wireOp",EDGE,"E18"),sQuery(id+"F0.wireOp",EDGE,"E19"),sQuery(id+"F0.wireOp",EDGE,"E20"),sQuery(id+"F0.wireOp",EDGE,"E25"),sQuery(id+"F0.wireOp",EDGE,"E26"),sQuery(id+"F0.wireOp",EDGE,"E27"),sQuery(id+"F0.wireOp",EDGE,"E28"),sQuery(id+"F0.wireOp",EDGE,"E29")])],"isStart":false});
            var Q21;
            {var subQ11=sQuery(id+"F0.wireOp",EDGE,"E11");Q21=makeQuery(id+"F0.imprint","IMPRINT",FACE,{"disambiguationData":[TD([[makeQuery(id+"F0.imprint","IMPRINT",EDGE,{"derivedFrom":subQ11}),-1.0]])]});}
            var Q22;
            {var subQ0=sQuery(id+"F0.wireOp",EDGE,"E12");Q22=makeQuery(id+"F0.imprint","IMPRINT",FACE,{"disambiguationData":[TD([[makeQuery(id+"F0.imprint","IMPRINT",EDGE,{"derivedFrom":subQ0}),1.0]])]});}
            var Q23;
            Q23=makeQuery(id+"F0.imprint","IMPRINT",FACE,{"disambiguationData":[TD([[makeQuery(id+"F0.imprint","IMPRINT",EDGE,{"derivedFrom":sQuery(id+"F0.wireOp",EDGE,"E30")}),-1.0]])]});
            var Q24;
            {var subQ0=sQuery(id+"F0.wireOp",EDGE,"E11");Q24=makeQuery(id+"F0.imprint","IMPRINT",FACE,{"disambiguationData":[TD([[makeQuery(id+"F0.imprint","IMPRINT",EDGE,{"derivedFrom":subQ0}),1.0]])]});}
            var Q25;
            {var subQ0=sQuery(id+"F0.wireOp",EDGE,"E31");var subQ1=sQuery(id+"F0.wireOp",EDGE,"E9");var subQ2=makeQuery(id+"F0.imprint","INTERSECT",VERTEX,{"disambiguationData":[OD(0.0)],"derivedFrom":[subQ1,subQ0]});Q25=makeQuery(id+"F0.imprint","IMPRINT",FACE,{"disambiguationData":[TD([[makeQuery(id+"F0.imprint","IMPRINT",EDGE,{"disambiguationData":[TD([[subQ2,-1.0]])],"derivedFrom":subQ1}),-1.0]])]});}
            var Q26;
            {var subQ1=sQuery(id+"F0.wireOp",EDGE,"E3");var subQ7=sQuery(id+"F0.wireOp",EDGE,"E25");var subQ8=makeQuery(id+"F0.imprint","INTERSECT",VERTEX,{"disambiguationData":[OD(0.0)],"derivedFrom":[subQ1,subQ7]});Q26=makeQuery(id+"F0.imprint","IMPRINT",FACE,{"disambiguationData":[TD([[makeQuery(id+"F0.imprint","IMPRINT",EDGE,{"disambiguationData":[TD([[subQ8,-1.0]])],"derivedFrom":subQ1}),-1.0]])]});}
            var Q27;
            {var subQ1=sQuery(id+"F0.wireOp",EDGE,"E3");var subQ5=sQuery(id+"F0.wireOp",EDGE,"E29");var subQ6=makeQuery(id+"F0.imprint","INTERSECT",VERTEX,{"disambiguationData":[OD(1.0)],"derivedFrom":[subQ1,subQ5]});Q27=makeQuery(id+"F0.imprint","IMPRINT",FACE,{"disambiguationData":[TD([[makeQuery(id+"F0.imprint","IMPRINT",EDGE,{"disambiguationData":[TD([[subQ6,-1.0]])],"derivedFrom":subQ1}),-1.0]])]});}
            var Q28;
            {var subQ0=sQuery(id+"F0.wireOp",EDGE,"E29");var subQ1=sQuery(id+"F0.wireOp",EDGE,"E9");var subQ2=makeQuery(id+"F0.imprint","INTERSECT",VERTEX,{"disambiguationData":[OD(1.0)],"derivedFrom":[subQ1,subQ0]});Q28=makeQuery(id+"F0.imprint","IMPRINT",FACE,{"disambiguationData":[TD([[makeQuery(id+"F0.imprint","IMPRINT",EDGE,{"disambiguationData":[TD([[subQ2,-1.0]])],"derivedFrom":subQ1}),-1.0]])]});}
            var Q29;
            {var subQ0=sQuery(id+"F0.wireOp",EDGE,"E29");var subQ1=sQuery(id+"F0.wireOp",EDGE,"E10");var subQ2=makeQuery(id+"F0.imprint","INTERSECT",VERTEX,{"disambiguationData":[OD(1.0)],"derivedFrom":[subQ1,subQ0]});Q29=makeQuery(id+"F0.imprint","IMPRINT",FACE,{"disambiguationData":[TD([[makeQuery(id+"F0.imprint","IMPRINT",EDGE,{"disambiguationData":[TD([[subQ2,-1.0]])],"derivedFrom":subQ1}),-1.0]])]});}
            var Q30;
            {var subQ0=sQuery(id+"F0.wireOp",EDGE,"E31");var subQ1=sQuery(id+"F0.wireOp",EDGE,"E10");var subQ2=makeQuery(id+"F0.imprint","INTERSECT",VERTEX,{"disambiguationData":[OD(0.0)],"derivedFrom":[subQ1,subQ0]});Q30=makeQuery(id+"F0.imprint","IMPRINT",FACE,{"disambiguationData":[TD([[makeQuery(id+"F0.imprint","IMPRINT",EDGE,{"disambiguationData":[TD([[subQ2,-1.0]])],"derivedFrom":subQ1}),-1.0]])]});}
            var Q31;
            {var subQ0=sQuery(id+"F0.wireOp",EDGE,"E31");var subQ1=sQuery(id+"F0.wireOp",EDGE,"E22");var subQ2=makeQuery(id+"F0.imprint","INTERSECT",VERTEX,{"disambiguationData":[OD(0.0)],"derivedFrom":[subQ1,subQ0]});Q31=makeQuery(id+"F0.imprint","IMPRINT",FACE,{"disambiguationData":[TD([[makeQuery(id+"F0.imprint","IMPRINT",EDGE,{"disambiguationData":[TD([[subQ2,-1.0]])],"derivedFrom":subQ1}),-1.0]])]});}
            var Q32;
            {var subQ0=sQuery(id+"F0.wireOp",EDGE,"E29");var subQ1=sQuery(id+"F0.wireOp",EDGE,"E3");var subQ2=makeQuery(id+"F0.imprint","INTERSECT",VERTEX,{"disambiguationData":[OD(1.0)],"derivedFrom":[subQ1,subQ0]});Q32=makeQuery(id+"F0.imprint","IMPRINT",FACE,{"disambiguationData":[TD([[makeQuery(id+"F0.imprint","IMPRINT",EDGE,{"disambiguationData":[TD([[subQ2,-1.0]])],"derivedFrom":subQ1}),1.0]])]});}
            var Q33;
            {var subQ7=sQuery(id+"F0.wireOp",EDGE,"E31");var subQ8=sQuery(id+"F0.wireOp",EDGE,"E0");var subQ9=makeQuery(id+"F0.imprint","INTERSECT",VERTEX,{"disambiguationData":[OD(0.0)],"derivedFrom":[subQ8,subQ7]});Q33=makeQuery(id+"F0.imprint","IMPRINT",FACE,{"disambiguationData":[TD([[makeQuery(id+"F0.imprint","IMPRINT",EDGE,{"disambiguationData":[TD([[subQ9,-1.0]])],"derivedFrom":subQ8}),-1.0]])]});}
            extrude(context, id + "F2", {"entities" : qUnion([Q0, Q1, Q2, Q3, Q4, Q5, Q6, Q7, Q8, Q9, Q10, Q11, Q12, Q13, Q14, Q15, Q16, Q17, Q18, Q19, Q20, Q21, Q22, Q23, Q24, Q25, Q26, Q27, Q28, Q29, Q30, Q31, Q32, Q33]), "oppositeDirection" : true, "depth" : 2 * mm});
        }
        {
            var Q0;
            {var subQ0=sQuery(id+"F0.wireOp",EDGE,"E12");Q0=makeQuery(id+"F0.imprint","IMPRINT",FACE,{"disambiguationData":[TD([[makeQuery(id+"F0.imprint","IMPRINT",EDGE,{"derivedFrom":subQ0}),1.0]])]});}
            var Q1;
            Q1=makeQuery(id+"F0.imprint","IMPRINT",FACE,{"disambiguationData":[TD([[makeQuery(id+"F0.imprint","IMPRINT",EDGE,{"derivedFrom":sQuery(id+"F0.wireOp",EDGE,"E30")}),-1.0]])]});
            var Q2;
            {var subQ0=sQuery(id+"F0.wireOp",EDGE,"E11");Q2=makeQuery(id+"F0.imprint","IMPRINT",FACE,{"disambiguationData":[TD([[makeQuery(id+"F0.imprint","IMPRINT",EDGE,{"derivedFrom":subQ0}),1.0]])]});}
            var Q3;
            {var subQ15=sQuery(id+"F0.wireOp",EDGE,"E12");Q3=makeQuery(id+"F0.imprint","IMPRINT",FACE,{"disambiguationData":[TD([[makeQuery(id+"F0.imprint","IMPRINT",EDGE,{"derivedFrom":subQ15}),-1.0]])]});}
            var Q4;
            {var subQ1=sQuery(id+"F0.wireOp",EDGE,"E21");var subQ5=sQuery(id+"F0.wireOp",EDGE,"E3");var subQ6=makeQuery(id+"F0.imprint","INTERSECT",VERTEX,{"disambiguationData":[OD(0.0)],"derivedFrom":[subQ5,subQ1]});Q4=makeQuery(id+"F0.imprint","IMPRINT",FACE,{"disambiguationData":[TD([[makeQuery(id+"F0.imprint","IMPRINT",EDGE,{"disambiguationData":[TD([[subQ6,-1.0]])],"derivedFrom":subQ5}),-1.0]])]});}
            var Q5;
            {var subQ1=sQuery(id+"F0.wireOp",EDGE,"E22");Q5=makeQuery(id+"F0.imprint","IMPRINT",FACE,{"disambiguationData":[TD([[makeQuery(id+"F0.imprint","IMPRINT",EDGE,{"derivedFrom":subQ1}),1.0]])]});}
            var Q6;
            {var subQ0=sQuery(id+"F0.wireOp",EDGE,"E28");var subQ1=sQuery(id+"F0.wireOp",EDGE,"E5");var subQ2=makeQuery(id+"F0.imprint","INTERSECT",VERTEX,{"disambiguationData":[OD(0.0)],"derivedFrom":[subQ1,subQ0]});Q6=makeQuery(id+"F0.imprint","IMPRINT",FACE,{"disambiguationData":[TD([[makeQuery(id+"F0.imprint","IMPRINT",EDGE,{"disambiguationData":[TD([[subQ2,-1.0]])],"derivedFrom":subQ1}),1.0]])]});}
            var Q7;
            {var subQ11=sQuery(id+"F0.wireOp",EDGE,"E11");Q7=makeQuery(id+"F0.imprint","IMPRINT",FACE,{"disambiguationData":[TD([[makeQuery(id+"F0.imprint","IMPRINT",EDGE,{"derivedFrom":subQ11}),-1.0]])]});}
            var Q8;
            {var subQ0=sQuery(id+"F0.wireOp",EDGE,"E29");var subQ1=sQuery(id+"F0.wireOp",EDGE,"E3");var subQ2=makeQuery(id+"F0.imprint","INTERSECT",VERTEX,{"disambiguationData":[OD(0.0)],"derivedFrom":[subQ1,subQ0]});Q8=makeQuery(id+"F0.imprint","IMPRINT",FACE,{"disambiguationData":[TD([[makeQuery(id+"F0.imprint","IMPRINT",EDGE,{"disambiguationData":[TD([[subQ2,-1.0]])],"derivedFrom":subQ1}),-1.0]])]});}
            var Q9;
            {var subQ0=sQuery(id+"F0.wireOp",EDGE,"E29");var subQ1=sQuery(id+"F0.wireOp",EDGE,"E3");var subQ2=makeQuery(id+"F0.imprint","INTERSECT",VERTEX,{"disambiguationData":[OD(0.0)],"derivedFrom":[subQ1,subQ0]});Q9=makeQuery(id+"F0.imprint","IMPRINT",FACE,{"disambiguationData":[TD([[makeQuery(id+"F0.imprint","IMPRINT",EDGE,{"disambiguationData":[TD([[subQ2,-1.0]])],"derivedFrom":subQ1}),1.0]])]});}
            var Q10;
            {var subQ5=sQuery(id+"F0.wireOp",EDGE,"E25");var subQ6=sQuery(id+"F0.wireOp",EDGE,"E3");var subQ7=makeQuery(id+"F0.imprint","INTERSECT",VERTEX,{"disambiguationData":[OD(1.0)],"derivedFrom":[subQ6,subQ5]});Q10=makeQuery(id+"F0.imprint","IMPRINT",FACE,{"disambiguationData":[TD([[makeQuery(id+"F0.imprint","IMPRINT",EDGE,{"disambiguationData":[TD([[subQ7,-1.0]])],"derivedFrom":subQ6}),-1.0]])]});}
            var Q11;
            {var subQ0=sQuery(id+"F0.wireOp",EDGE,"E27");var subQ1=sQuery(id+"F0.wireOp",EDGE,"E4");var subQ2=makeQuery(id+"F0.imprint","INTERSECT",VERTEX,{"disambiguationData":[OD(0.0)],"derivedFrom":[subQ1,subQ0]});Q11=makeQuery(id+"F0.imprint","IMPRINT",FACE,{"disambiguationData":[TD([[makeQuery(id+"F0.imprint","IMPRINT",EDGE,{"disambiguationData":[TD([[subQ2,-1.0]])],"derivedFrom":subQ1}),1.0]])]});}
            var Q12;
            {var subQ0=sQuery(id+"F0.wireOp",EDGE,"E29");var subQ1=sQuery(id+"F0.wireOp",EDGE,"E9");var subQ2=makeQuery(id+"F0.imprint","INTERSECT",VERTEX,{"disambiguationData":[OD(1.0)],"derivedFrom":[subQ1,subQ0]});Q12=makeQuery(id+"F0.imprint","IMPRINT",FACE,{"disambiguationData":[TD([[makeQuery(id+"F0.imprint","IMPRINT",EDGE,{"disambiguationData":[TD([[subQ2,-1.0]])],"derivedFrom":subQ1}),-1.0]])]});}
            var Q13;
            {var subQ1=sQuery(id+"F0.wireOp",EDGE,"E3");var subQ5=sQuery(id+"F0.wireOp",EDGE,"E29");var subQ6=makeQuery(id+"F0.imprint","INTERSECT",VERTEX,{"disambiguationData":[OD(1.0)],"derivedFrom":[subQ1,subQ5]});Q13=makeQuery(id+"F0.imprint","IMPRINT",FACE,{"disambiguationData":[TD([[makeQuery(id+"F0.imprint","IMPRINT",EDGE,{"disambiguationData":[TD([[subQ6,-1.0]])],"derivedFrom":subQ1}),-1.0]])]});}
            var Q14;
            {var subQ7=sQuery(id+"F0.wireOp",EDGE,"E3");var subQ9=sQuery(id+"F0.wireOp",EDGE,"E31");var subQ10=makeQuery(id+"F0.imprint","INTERSECT",VERTEX,{"disambiguationData":[OD(1.0)],"derivedFrom":[subQ7,subQ9]});Q14=makeQuery(id+"F0.imprint","IMPRINT",FACE,{"disambiguationData":[TD([[makeQuery(id+"F0.imprint","IMPRINT",EDGE,{"disambiguationData":[TD([[subQ10,-1.0]])],"derivedFrom":subQ7}),-1.0]])]});}
            var Q15;
            {var subQ0=sQuery(id+"F0.wireOp",EDGE,"E29");var subQ1=sQuery(id+"F0.wireOp",EDGE,"E10");var subQ2=makeQuery(id+"F0.imprint","INTERSECT",VERTEX,{"disambiguationData":[OD(1.0)],"derivedFrom":[subQ1,subQ0]});Q15=makeQuery(id+"F0.imprint","IMPRINT",FACE,{"disambiguationData":[TD([[makeQuery(id+"F0.imprint","IMPRINT",EDGE,{"disambiguationData":[TD([[subQ2,-1.0]])],"derivedFrom":subQ1}),-1.0]])]});}
            var Q16;
            {var subQ0=sQuery(id+"F0.wireOp",EDGE,"E31");var subQ1=sQuery(id+"F0.wireOp",EDGE,"E10");var subQ2=makeQuery(id+"F0.imprint","INTERSECT",VERTEX,{"disambiguationData":[OD(0.0)],"derivedFrom":[subQ1,subQ0]});Q16=makeQuery(id+"F0.imprint","IMPRINT",FACE,{"disambiguationData":[TD([[makeQuery(id+"F0.imprint","IMPRINT",EDGE,{"disambiguationData":[TD([[subQ2,-1.0]])],"derivedFrom":subQ1}),-1.0]])]});}
            var Q17;
            {var subQ0=sQuery(id+"F0.wireOp",EDGE,"E31");var subQ1=sQuery(id+"F0.wireOp",EDGE,"E9");var subQ2=makeQuery(id+"F0.imprint","INTERSECT",VERTEX,{"disambiguationData":[OD(0.0)],"derivedFrom":[subQ1,subQ0]});Q17=makeQuery(id+"F0.imprint","IMPRINT",FACE,{"disambiguationData":[TD([[makeQuery(id+"F0.imprint","IMPRINT",EDGE,{"disambiguationData":[TD([[subQ2,-1.0]])],"derivedFrom":subQ1}),-1.0]])]});}
            var Q18;
            {var subQ1=sQuery(id+"F0.wireOp",EDGE,"E3");var subQ7=sQuery(id+"F0.wireOp",EDGE,"E25");var subQ8=makeQuery(id+"F0.imprint","INTERSECT",VERTEX,{"disambiguationData":[OD(0.0)],"derivedFrom":[subQ1,subQ7]});Q18=makeQuery(id+"F0.imprint","IMPRINT",FACE,{"disambiguationData":[TD([[makeQuery(id+"F0.imprint","IMPRINT",EDGE,{"disambiguationData":[TD([[subQ8,-1.0]])],"derivedFrom":subQ1}),-1.0]])]});}
            var Q19;
            {var subQ0=sQuery(id+"F0.wireOp",EDGE,"E31");var subQ1=sQuery(id+"F0.wireOp",EDGE,"E3");var subQ2=makeQuery(id+"F0.imprint","INTERSECT",VERTEX,{"disambiguationData":[OD(0.0)],"derivedFrom":[subQ1,subQ0]});Q19=makeQuery(id+"F0.imprint","IMPRINT",FACE,{"disambiguationData":[TD([[makeQuery(id+"F0.imprint","IMPRINT",EDGE,{"disambiguationData":[TD([[subQ2,-1.0]])],"derivedFrom":subQ1}),-1.0]])]});}
            var Q20;
            {var subQ0=sQuery(id+"F0.wireOp",EDGE,"E29");var subQ1=sQuery(id+"F0.wireOp",EDGE,"E10");var subQ2=makeQuery(id+"F0.imprint","INTERSECT",VERTEX,{"disambiguationData":[OD(0.0)],"derivedFrom":[subQ1,subQ0]});Q20=makeQuery(id+"F0.imprint","IMPRINT",FACE,{"disambiguationData":[TD([[makeQuery(id+"F0.imprint","IMPRINT",EDGE,{"disambiguationData":[TD([[subQ2,-1.0]])],"derivedFrom":subQ1}),-1.0]])]});}
            var Q21;
            {var subQ0=sQuery(id+"F0.wireOp",EDGE,"E29");var subQ1=sQuery(id+"F0.wireOp",EDGE,"E3");var subQ2=makeQuery(id+"F0.imprint","INTERSECT",VERTEX,{"disambiguationData":[OD(1.0)],"derivedFrom":[subQ1,subQ0]});Q21=makeQuery(id+"F0.imprint","IMPRINT",FACE,{"disambiguationData":[TD([[makeQuery(id+"F0.imprint","IMPRINT",EDGE,{"disambiguationData":[TD([[subQ2,-1.0]])],"derivedFrom":subQ1}),1.0]])]});}
            var Q22;
            {var subQ0=sQuery(id+"F0.wireOp",EDGE,"E25");var subQ1=sQuery(id+"F0.wireOp",EDGE,"E3");var subQ2=makeQuery(id+"F0.imprint","INTERSECT",VERTEX,{"disambiguationData":[OD(0.0)],"derivedFrom":[subQ1,subQ0]});Q22=makeQuery(id+"F0.imprint","IMPRINT",FACE,{"disambiguationData":[TD([[makeQuery(id+"F0.imprint","IMPRINT",EDGE,{"disambiguationData":[TD([[subQ2,-1.0]])],"derivedFrom":subQ1}),1.0]])]});}
            extrude(context, id + "F3", {"entities" : qUnion([Q0, Q1, Q2, Q3, Q4, Q5, Q6, Q7, Q8, Q9, Q10, Q11, Q12, Q13, Q14, Q15, Q16, Q17, Q18, Q19, Q20, Q21, Q22]), "depth" : 10 * mm});
        }
        {
            var Q0;
            Q0=makeQuery(id+"F0.imprint","IMPRINT",FACE,{"disambiguationData":[TD([[makeQuery(id+"F0.imprint","IMPRINT",EDGE,{"derivedFrom":sQuery(id+"F0.wireOp",EDGE,"E30")}),-1.0]])]});
            var Q1;
            {var subQ0=sQuery(id+"F0.wireOp",EDGE,"E29");var subQ1=sQuery(id+"F0.wireOp",EDGE,"E10");var subQ2=makeQuery(id+"F0.imprint","INTERSECT",VERTEX,{"disambiguationData":[OD(0.0)],"derivedFrom":[subQ1,subQ0]});Q1=makeQuery(id+"F0.imprint","IMPRINT",FACE,{"disambiguationData":[TD([[makeQuery(id+"F0.imprint","IMPRINT",EDGE,{"disambiguationData":[TD([[subQ2,-1.0]])],"derivedFrom":subQ1}),-1.0]])]});}
            var Q2;
            {var subQ0=sQuery(id+"F0.wireOp",EDGE,"E29");var subQ1=sQuery(id+"F0.wireOp",EDGE,"E3");var subQ2=makeQuery(id+"F0.imprint","INTERSECT",VERTEX,{"disambiguationData":[OD(0.0)],"derivedFrom":[subQ1,subQ0]});Q2=makeQuery(id+"F0.imprint","IMPRINT",FACE,{"disambiguationData":[TD([[makeQuery(id+"F0.imprint","IMPRINT",EDGE,{"disambiguationData":[TD([[subQ2,-1.0]])],"derivedFrom":subQ1}),-1.0]])]});}
            var Q3;
            {var subQ0=sQuery(id+"F0.wireOp",EDGE,"E29");var subQ1=sQuery(id+"F0.wireOp",EDGE,"E3");var subQ2=makeQuery(id+"F0.imprint","INTERSECT",VERTEX,{"disambiguationData":[OD(0.0)],"derivedFrom":[subQ1,subQ0]});Q3=makeQuery(id+"F0.imprint","IMPRINT",FACE,{"disambiguationData":[TD([[makeQuery(id+"F0.imprint","IMPRINT",EDGE,{"disambiguationData":[TD([[subQ2,-1.0]])],"derivedFrom":subQ1}),1.0]])]});}
            extrude(context, id + "F4", {"entities" : qUnion([Q0, Q1, Q2, Q3]), "depth" : 39 * mm});
        }
        {
            var Q0;
            {var subQ0=sQuery(id+"F0.wireOp",EDGE,"E24");Q0=makeQuery(id+"F3.opExtrude","CAP_EDGE",EDGE,{"disambiguationData":[OSD([subQ0]),TDD([makeQuery(id+"F0.imprint","IMPRINT",EDGE,{"disambiguationData":[TD([[makeQuery(id+"F0.imprint","INTERSECT",VERTEX,{"derivedFrom":[sQuery(id+"F0.wireOp",EDGE,"E21"),subQ0]}),-1.0]])],"derivedFrom":subQ0})])],"isStart":false});}
            var Q1;
            {var subQ0=sQuery(id+"F0.wireOp",EDGE,"E5");Q1=makeQuery(id+"F3.opExtrude","CAP_EDGE",EDGE,{"disambiguationData":[OSD([subQ0]),TDD([makeQuery(id+"F0.imprint","IMPRINT",EDGE,{"disambiguationData":[TD([[makeQuery(id+"F0.imprint","INTERSECT",VERTEX,{"disambiguationData":[OD(1.0)],"derivedFrom":[subQ0,sQuery(id+"F0.wireOp",EDGE,"E28")]}),-1.0]])],"derivedFrom":subQ0})])],"isStart":false});}
            var Q2;
            Q2=makeQuery(id+"F3.opExtrude","CAP_EDGE",EDGE,{"disambiguationData":[OSD([sQuery(id+"F0.wireOp",EDGE,"E28")])],"isStart":false});
            var Q3;
            {var subQ0=sQuery(id+"F0.wireOp",EDGE,"E5");Q3=makeQuery(id+"F3.opExtrude","CAP_EDGE",EDGE,{"disambiguationData":[OSD([subQ0]),TDD([makeQuery(id+"F0.imprint","IMPRINT",EDGE,{"disambiguationData":[TD([[makeQuery(id+"F0.imprint","INTERSECT",VERTEX,{"disambiguationData":[OD(0.0)],"derivedFrom":[subQ0,sQuery(id+"F0.wireOp",EDGE,"E28")]}),1.0]])],"derivedFrom":subQ0})])],"isStart":false});}
            var Q4;
            Q4=makeQuery(id+"F3.opExtrude","CAP_EDGE",EDGE,{"disambiguationData":[OSD([sQuery(id+"F0.wireOp",EDGE,"E22")])],"isStart":false});
            var Q5;
            {var subQ0=sQuery(id+"F0.wireOp",EDGE,"E23");Q5=makeQuery(id+"F3.opExtrude","CAP_EDGE",EDGE,{"disambiguationData":[OSD([subQ0]),TDD([makeQuery(id+"F0.imprint","IMPRINT",EDGE,{"disambiguationData":[TD([[makeQuery(id+"F0.imprint","INTERSECT",VERTEX,{"derivedFrom":[sQuery(id+"F0.wireOp",EDGE,"E21"),subQ0]}),1.0]])],"derivedFrom":subQ0})])],"isStart":false});}
            var Q6;
            {var subQ0=sQuery(id+"F0.wireOp",EDGE,"E21");Q6=makeQuery(id+"F3.opExtrude","CAP_EDGE",EDGE,{"disambiguationData":[OSD([subQ0]),TDD([makeQuery(id+"F0.imprint","IMPRINT",EDGE,{"disambiguationData":[TD([[makeQuery(id+"F0.imprint","INTERSECT",VERTEX,{"derivedFrom":[subQ0,sQuery(id+"F0.wireOp",EDGE,"E23")]}),1.0]])],"derivedFrom":subQ0})])],"isStart":false});}
            var Q7;
            {var subQ0=sQuery(id+"F0.wireOp",EDGE,"E3");var subQ1=makeQuery(id+"F0.imprint","INTERSECT",VERTEX,{"disambiguationData":[OD(1.0)],"derivedFrom":[subQ0,sQuery(id+"F0.wireOp",EDGE,"E25")]});Q7=makeQuery(id+"F3.opExtrude","CAP_EDGE",EDGE,{"disambiguationData":[OSD([subQ0]),TDD([makeQuery(id+"F0.imprint","IMPRINT",EDGE,{"disambiguationData":[TD([[makeQuery(id+"F0.imprint","INTERSECT",VERTEX,{"disambiguationData":[OD(1.0)],"derivedFrom":[subQ0,sQuery(id+"F0.wireOp",EDGE,"E29")]}),-1.0]])],"derivedFrom":subQ0}),makeQuery(id+"F0.imprint","IMPRINT",EDGE,{"disambiguationData":[TD([[subQ1,-1.0]])],"derivedFrom":subQ0})])],"isStart":false});}
            var Q8;
            {var subQ0=sQuery(id+"F0.wireOp",EDGE,"E3");var subQ1=makeQuery(id+"F0.imprint","INTERSECT",VERTEX,{"disambiguationData":[OD(0.0)],"derivedFrom":[subQ0,sQuery(id+"F0.wireOp",EDGE,"E25")]});Q8=makeQuery(id+"F3.opExtrude","CAP_EDGE",EDGE,{"disambiguationData":[OSD([subQ0]),TDD([makeQuery(id+"F0.imprint","IMPRINT",EDGE,{"disambiguationData":[TD([[makeQuery(id+"F0.imprint","INTERSECT",VERTEX,{"disambiguationData":[OD(0.0)],"derivedFrom":[subQ0,sQuery(id+"F0.wireOp",EDGE,"E21")]}),-1.0]])],"derivedFrom":subQ0}),makeQuery(id+"F0.imprint","IMPRINT",EDGE,{"disambiguationData":[TD([[subQ1,-1.0]])],"derivedFrom":subQ0})])],"isStart":false});}
            var Q9;
            {var subQ0=sQuery(id+"F0.wireOp",EDGE,"E21");Q9=makeQuery(id+"F3.opExtrude","CAP_EDGE",EDGE,{"disambiguationData":[OSD([subQ0]),TDD([makeQuery(id+"F0.imprint","IMPRINT",EDGE,{"disambiguationData":[TD([[makeQuery(id+"F0.imprint","INTERSECT",VERTEX,{"derivedFrom":[subQ0,sQuery(id+"F0.wireOp",EDGE,"E24")]}),-1.0]])],"derivedFrom":subQ0})])],"isStart":false});}
            var Q10;
            Q10=makeQuery(id+"F3.opExtrude","CAP_EDGE",EDGE,{"disambiguationData":[OSD([sQuery(id+"F0.wireOp",EDGE,"E27")])],"isStart":false});
            var Q11;
            {var subQ0=sQuery(id+"F0.wireOp",EDGE,"E4");Q11=makeQuery(id+"F3.opExtrude","CAP_EDGE",EDGE,{"disambiguationData":[OSD([subQ0]),TDD([makeQuery(id+"F0.imprint","IMPRINT",EDGE,{"disambiguationData":[TD([[makeQuery(id+"F0.imprint","INTERSECT",VERTEX,{"disambiguationData":[OD(0.0)],"derivedFrom":[subQ0,sQuery(id+"F0.wireOp",EDGE,"E23")]}),-1.0]])],"derivedFrom":subQ0})])],"isStart":false});}
            var Q12;
            {var subQ0=sQuery(id+"F0.wireOp",EDGE,"E4");Q12=makeQuery(id+"F3.opExtrude","CAP_EDGE",EDGE,{"disambiguationData":[OSD([subQ0]),TDD([makeQuery(id+"F0.imprint","IMPRINT",EDGE,{"disambiguationData":[TD([[makeQuery(id+"F0.imprint","INTERSECT",VERTEX,{"disambiguationData":[OD(1.0)],"derivedFrom":[subQ0,sQuery(id+"F0.wireOp",EDGE,"E27")]}),-1.0]])],"derivedFrom":subQ0})])],"isStart":false});}
            fillet(context, id + "F5", {"entities" : qUnion([Q0, Q1, Q2, Q3, Q4, Q5, Q6, Q7, Q8, Q9, Q10, Q11, Q12]), "radius" : 2 * mm, "tangentPropagation" : true, "allowEdgeOverflow" : false});
        }
        {
            var Q0;
            {var subQ0=sQuery(id+"F0.wireOp",EDGE,"E31");var subQ1=sQuery(id+"F0.wireOp",EDGE,"E9");var subQ2=makeQuery(id+"F0.imprint","INTERSECT",VERTEX,{"disambiguationData":[OD(0.0)],"derivedFrom":[subQ1,subQ0]});Q0=makeQuery(id+"F0.imprint","IMPRINT",FACE,{"disambiguationData":[TD([[makeQuery(id+"F0.imprint","IMPRINT",EDGE,{"disambiguationData":[TD([[subQ2,-1.0]])],"derivedFrom":subQ1}),-1.0]])]});}
            var Q1;
            {var subQ0=sQuery(id+"F0.wireOp",EDGE,"E31");var subQ1=sQuery(id+"F0.wireOp",EDGE,"E10");var subQ2=makeQuery(id+"F0.imprint","INTERSECT",VERTEX,{"disambiguationData":[OD(0.0)],"derivedFrom":[subQ1,subQ0]});Q1=makeQuery(id+"F0.imprint","IMPRINT",FACE,{"disambiguationData":[TD([[makeQuery(id+"F0.imprint","IMPRINT",EDGE,{"disambiguationData":[TD([[subQ2,-1.0]])],"derivedFrom":subQ1}),-1.0]])]});}
            var Q2;
            {var subQ4=sQuery(id+"F0.wireOp",EDGE,"E31");var subQ7=sQuery(id+"F0.wireOp",EDGE,"E22");var subQ9=makeQuery(id+"F0.imprint","INTERSECT",VERTEX,{"disambiguationData":[OD(0.0)],"derivedFrom":[subQ7,subQ4]});Q2=makeQuery(id+"F0.imprint","IMPRINT",FACE,{"disambiguationData":[TD([[makeQuery(id+"F0.imprint","IMPRINT",EDGE,{"disambiguationData":[TD([[subQ9,-1.0]])],"derivedFrom":subQ7}),1.0]])]});}
            var Q3;
            {var subQ0=sQuery(id+"F0.wireOp",EDGE,"E29");var subQ1=sQuery(id+"F0.wireOp",EDGE,"E10");var subQ2=makeQuery(id+"F0.imprint","INTERSECT",VERTEX,{"disambiguationData":[OD(1.0)],"derivedFrom":[subQ1,subQ0]});Q3=makeQuery(id+"F0.imprint","IMPRINT",FACE,{"disambiguationData":[TD([[makeQuery(id+"F0.imprint","IMPRINT",EDGE,{"disambiguationData":[TD([[subQ2,-1.0]])],"derivedFrom":subQ1}),-1.0]])]});}
            var Q4;
            {var subQ0=sQuery(id+"F0.wireOp",EDGE,"E29");var subQ1=sQuery(id+"F0.wireOp",EDGE,"E9");var subQ2=makeQuery(id+"F0.imprint","INTERSECT",VERTEX,{"disambiguationData":[OD(1.0)],"derivedFrom":[subQ1,subQ0]});Q4=makeQuery(id+"F0.imprint","IMPRINT",FACE,{"disambiguationData":[TD([[makeQuery(id+"F0.imprint","IMPRINT",EDGE,{"disambiguationData":[TD([[subQ2,-1.0]])],"derivedFrom":subQ1}),-1.0]])]});}
            var Q5;
            {var subQ1=sQuery(id+"F0.wireOp",EDGE,"E3");var subQ5=sQuery(id+"F0.wireOp",EDGE,"E29");var subQ6=makeQuery(id+"F0.imprint","INTERSECT",VERTEX,{"disambiguationData":[OD(1.0)],"derivedFrom":[subQ1,subQ5]});Q5=makeQuery(id+"F0.imprint","IMPRINT",FACE,{"disambiguationData":[TD([[makeQuery(id+"F0.imprint","IMPRINT",EDGE,{"disambiguationData":[TD([[subQ6,-1.0]])],"derivedFrom":subQ1}),-1.0]])]});}
            var Q6;
            {var subQ1=sQuery(id+"F0.wireOp",EDGE,"E3");var subQ7=sQuery(id+"F0.wireOp",EDGE,"E25");var subQ8=makeQuery(id+"F0.imprint","INTERSECT",VERTEX,{"disambiguationData":[OD(0.0)],"derivedFrom":[subQ1,subQ7]});Q6=makeQuery(id+"F0.imprint","IMPRINT",FACE,{"disambiguationData":[TD([[makeQuery(id+"F0.imprint","IMPRINT",EDGE,{"disambiguationData":[TD([[subQ8,-1.0]])],"derivedFrom":subQ1}),-1.0]])]});}
            extrude(context, id + "F6", {"entities" : qUnion([Q0, Q1, Q2, Q3, Q4, Q5, Q6]), "depth" : 14 * mm});
        }
        {
            var Q0;
            {var subQ0=sQuery(id+"F0.wireOp",EDGE,"E31");var subQ1=makeQuery(id+"F0.imprint","INTERSECT",VERTEX,{"disambiguationData":[OD(1.0)],"derivedFrom":[sQuery(id+"F0.wireOp",EDGE,"E9"),subQ0]});var subQ2=makeQuery(id+"F0.imprint","INTERSECT",VERTEX,{"disambiguationData":[OD(1.0)],"derivedFrom":[sQuery(id+"F0.wireOp",EDGE,"E10"),subQ0]});Q0=makeQuery(id+"F6.opExtrude","CAP_EDGE",EDGE,{"disambiguationData":[OSD([subQ0]),TDD([makeQuery(id+"F0.imprint","IMPRINT",EDGE,{"disambiguationData":[TD([[subQ1,-1.0]])],"derivedFrom":subQ0}),makeQuery(id+"F0.imprint","IMPRINT",EDGE,{"disambiguationData":[TD([[makeQuery(id+"F0.imprint","INTERSECT",VERTEX,{"disambiguationData":[OD(1.0)],"derivedFrom":[sQuery(id+"F0.wireOp",EDGE,"E22"),subQ0]}),-1.0]])],"derivedFrom":subQ0}),makeQuery(id+"F0.imprint","IMPRINT",EDGE,{"disambiguationData":[TD([[subQ2,1.0]])],"derivedFrom":subQ0}),makeQuery(id+"F0.imprint","IMPRINT",EDGE,{"disambiguationData":[TD([[subQ1,1.0]])],"derivedFrom":subQ0})])],"isStart":false});}
            fillet(context, id + "F7", {"entities" : qUnion([Q0]), "radius" : 4 * mm, "tangentPropagation" : true, "allowEdgeOverflow" : false});
        }
        {
            var Q0;
            {var subQ0=sQuery(id+"F0.wireOp",EDGE,"E30");Q0=makeQuery(id+"F2.opExtrude","CAP_EDGE",EDGE,{"disambiguationData":[OSD([subQ0]),TDD([makeQuery(id+"F0.imprint","IMPRINT",EDGE,{"derivedFrom":subQ0})])],"isStart":false});}
            fillet(context, id + "F8", {"entities" : qUnion([Q0]), "radius" : 4.8 * mm, "tangentPropagation" : true, "allowEdgeOverflow" : false});
        }
        {
            var Q0;
            Q0=qCreatedBy(makeId("Front.planeOp"),FACE);
            var sketch = newSketch(context, id + "F9", { "sketchPlane" : qUnion([Q0])});
            skCircle(sketch, "E32", {"center": v(15.95, 37.87) * mm, "radius": 1 * mm});
            skSolve(sketch);
        }
        {
            var Q0;
            Q0=sQuery(id+"F9.wireOp",EDGE,"E32");
            var Q1;
            Q1=sQuery(id+"F0.wireOp",EDGE,"E29");
            revolve(context, id + "F10", {"bodyType" : ToolBodyType.SURFACE, "surfaceEntities" : qUnion([Q0]), "axis" : qUnion([Q1]), "revolveType" : RevolveType.FULL});
        }
    });
